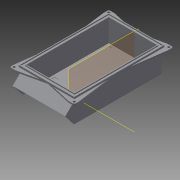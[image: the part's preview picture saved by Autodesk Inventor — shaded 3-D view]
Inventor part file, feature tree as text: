
AUTODESK INVENTOR PART (.ipt)
format: ipt  version: 2015 SP2 (Build 190223200, 223)  size: 392,704 bytes
history: native  units: in
note: dims shown in document units (in); Inventor stores cm internally (conversion verified against a paired STEP export)
features: sketch x19, extrude x15, mirror x6, projected_geometry x4, hole x3, plane x2, fillet x2
ambient origin geometry x8: Origin, YZ Plane, XZ Plane, XY Plane, X Axis, Y Axis, Z Axis, Center Point
bodies: Solid1 (feature_tree)
feature tree (51):
  extrude  "Extrusion1"  Depth=2.4937in
  extrude  "Extrusion3"  Depth=0.0591in TaperAngle=0.0deg
  extrude  "Extrusion4"  Depth=0.1969in
  extrude  "Extrusion5"  Depth=0.1969in
  plane  "Work Plane1"
  sketch  "Sketch5"  dims[d9=0.1969in d10=0.1969in]
  plane  "Work Plane5"
  extrude  "Extrusion6"  Depth=0.1969in
  extrude  "Extrusion7"  Depth=0.1969in
  mirror  "Mirror1"
  extrude  "Extrusion8"  Depth=0.1969in
  extrude  "Extrusion9"  Depth=0.0197in
  extrude  "Extrusion10"  Depth=0.0004in
  extrude  "Extrusion11"  Depth=1.1811in TaperAngle=0.0deg
  extrude  "Extrusion12"  Depth=0.0394in TaperAngle=0.0deg
  fillet  "Fillet1"  [1 undecoded]
  hole  "Hole1"  [1 undecoded]
  mirror  "Mirror2"
  extrude  "Extrusion13"  Depth=0.0394in TaperAngle=0.0deg
  extrude  "Extrusion14"  Depth=0.0394in
  extrude  "Extrusion15"  Depth=0.0394in
  mirror  "Mirror3"
  extrude  "Extrusion16"  Depth=0.0394in
  fillet  "Fillet3"  Radius=0.0394in
  mirror  "Mirror5"
  mirror  "Mirror6"
  hole  "Hole2"  [1 undecoded]
  mirror  "Mirror7"
  hole  "Hole3"  [1 undecoded]
  sketch  "Sketch1"  dims[d0=3.0937in d1=2.4937in]
  sketch  "Sketch2"  dims[d2=0.1181in d3=0.0591in d4=0.0in]
  projected_geometry  "Projected Loop1"
  sketch  "Sketch3"  dims[d5=0.1181in d6=0.1969in]
  projected_geometry  "Projected Loop2"
  sketch  "Sketch4"  dims[d7=0.1969in d8=0.1969in]
  sketch  "Sketch6"  dims[d11=0.1969in d12=0.1969in]
  sketch  "Sketch7"  dims[d13=0.1969in d16=0.0004in]
  sketch  "Sketch8"  dims[d17=0.0197in d18=0.0in d19=0.0004in]
  sketch  "Sketch9"  dims[d20=0.0004in d21=0.0004in]
  sketch  "Sketch10"  dims[d22=0.0394in d23=1.1811in d24=0.0591in d25=0.0in d26=0.0in]
  projected_geometry  "Projected Loop3"
  sketch  "Sketch11"  dims[d27=0.0591in d28=0.0394in d29=0.0in d30=-1.4043in]
  sketch  "Sketch13"  dims[d32=135.0deg d33=0.0394in d34=0.0in]
  sketch  "Sketch14"  dims[d35=0.0394in d36=0.0in d37=0.0394in d38=0.0in]
  sketch  "Sketch15"  dims[d39=0.0394in d40=0.0394in]
  projected_geometry  "Projected Loop4"
  sketch  "Sketch16"  dims[d41=0.0394in d42=0.0394in]
  sketch  "Sketch17"  dims[d43=0.0394in d44=0.0in d45=0.0394in d46=0.0394in]
  sketch  "Sketch18"  dims[d47=0.0591in d48=0.0in d49=0.315in]
  sketch  "Sketch19"  dims[d50=0.315in d51=0.2362in]
  sketch  "Sketch20"  dims[d52=0.2362in d53=4.6488in d54=2.3244in d55=2.8087in d56=1.4043in d57=0.0787in d58=0.0in d59=0.0787in d60=0.0in d61=0.0787in d62=0.0787in d63=0.0in d64=0.2362in d65=0.1181in d66=0.1181in d67=0.2362in d68=0.1575in d69=0.0787in d70=90.0deg d71=0.315in d72=0.8108in d73=0.0787in d74=0.7874in d75=0.0in d76=0.0787in d77=0.0in d80=0.315in d81=0.315in d82=0.2362in d83=0.2362in d84=0.0787in d85=0.0in d86=0.0787in d87=0.2362in d88=0.2362in d89=0.1181in d90=0.1181in d91=0.2362in d92=0.1575in d93=0.0787in d94=90.0deg d95=0.315in d96=0.8108in d97=2.8087in d98=0.3878in d99=1.4043in d100=0.3878in d101=0.2362in d102=0.1575in d103=0.0787in d104=90.0deg d105=0.315in d106=0.8108in d107=0.7874in d108=4.3964in]
note: 4 required parameter values undecoded (feature->parameter linkage not recoverable at this tier; creation-order binding heuristic only, values carry confidence <= 0.55)
